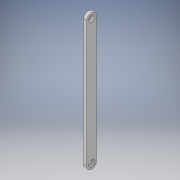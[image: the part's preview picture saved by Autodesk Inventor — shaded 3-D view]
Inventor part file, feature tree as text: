
AUTODESK INVENTOR PART (.ipt)
format: ipt  version: 2017 (Build 210142000, 142)  size: 101,888 bytes
history: native  units: in
note: dims shown in document units (in); Inventor stores cm internally (conversion verified against a paired STEP export)
features: extrude x1, sketch x1
ambient origin geometry x8: Origin, YZ Plane, XZ Plane, XY Plane, X Axis, Y Axis, Z Axis, Center Point
bodies: Solid1 (feature_tree)
feature tree (2):
  extrude  "Extrusion1"  Depth=0.77in
  sketch  "Sketch1"  dims[d0=0.5in d1=0.77in d2=9.682in d3=9.618in d4=0.5in d5=0.25in d6=0.0in]
